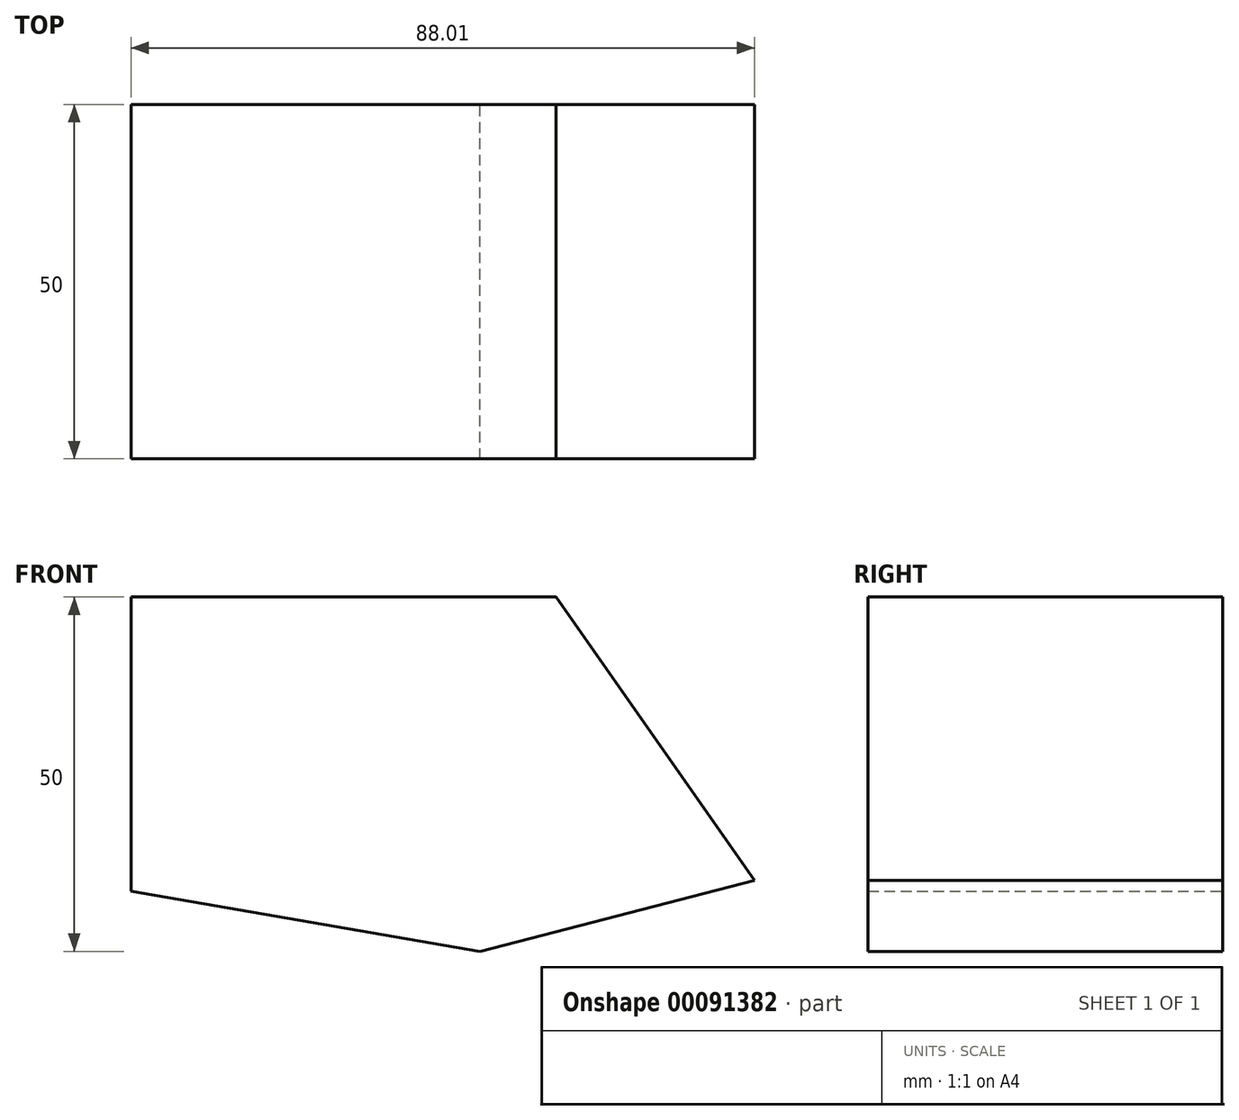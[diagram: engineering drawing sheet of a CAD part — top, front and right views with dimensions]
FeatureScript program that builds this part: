
annotation { "Feature Type Name" : "Feature", "Feature Type Description" : "" }
export const myFeature = defineFeature(function(context is Context, id is Id, definition is map)
    precondition{}
    {
        {
            var Q0;
            Q0=qCreatedBy(makeId("Front.planeOp"),FACE);
            var sketch = newSketch(context, id + "F0", { "sketchPlane" : qUnion([Q0])});
            skLineSegment(sketch, "E0", {"start": v(-30, 0) * mm, "end": v(-30, 25) * mm});
            skLineSegment(sketch, "E1", {"start": v(-30, 25) * mm, "end": v(30, 25) * mm});
            skLineSegment(sketch, "E2", {"start": v(30, 25) * mm, "end": v(58, -15) * mm});
            skLineSegment(sketch, "E3", {"start": v(58, -15) * mm, "end": v(19.28, -25) * mm});
            skLineSegment(sketch, "E4", {"start": v(19.28, -25) * mm, "end": v(-30, -16.54) * mm});
            skLineSegment(sketch, "E5", {"start": v(-30, -16.54) * mm, "end": v(-30, 0) * mm});
            skSolve(sketch);
        }
        {
            var Q0;
            Q0 = qSketchRegion(id + "F0", true);
            extrude(context, id + "F1", {"entities" : qUnion([Q0]), "depth" : 25 * mm, "hasSecondDirection" : true, "secondDirectionOppositeDirection" : true, "secondDirectionDepth" : 25 * mm});
        }
    });
